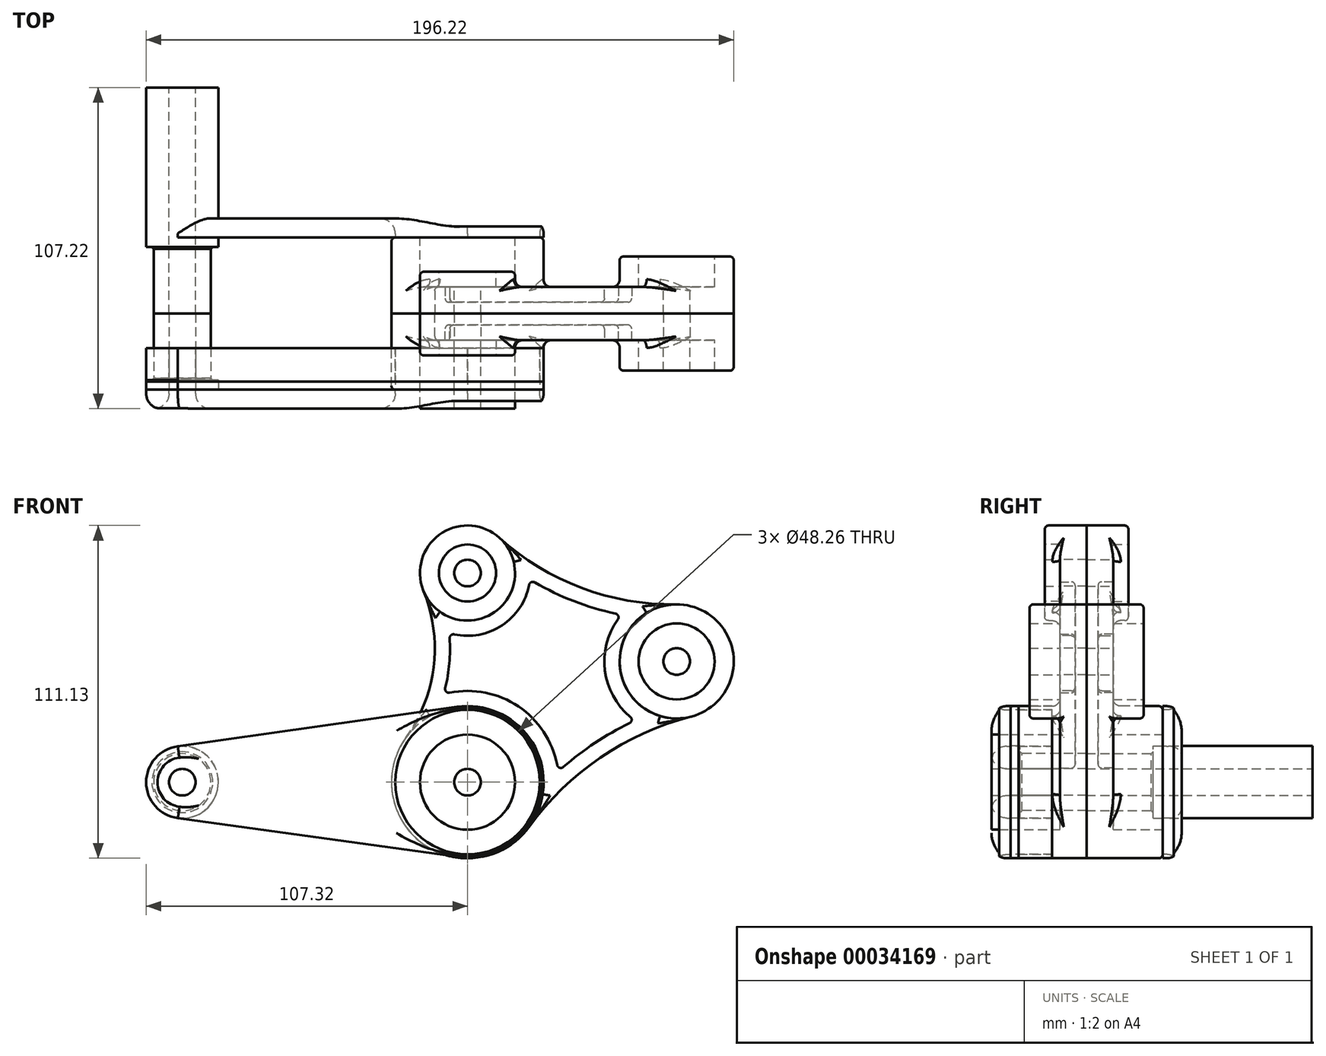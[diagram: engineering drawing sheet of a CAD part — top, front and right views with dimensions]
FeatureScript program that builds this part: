
annotation { "Feature Type Name" : "Feature", "Feature Type Description" : "" }
export const myFeature = defineFeature(function(context is Context, id is Id, definition is map)
    precondition{}
    {
        {
            var Q0;
            Q0=qCreatedBy(makeId("Front.planeOp"),FACE);
            var sketch = newSketch(context, id + "F0", { "sketchPlane" : qUnion([Q0])});
            skCircle(sketch, "E0", {"center": v(0, 0) * mm, "radius": 25.4 * mm});
            skCircle(sketch, "E1", {"center": v(0, 69.85) * mm, "radius": 15.88 * mm});
            skCircle(sketch, "E2", {"center": v(69.85, 40.33) * mm, "radius": 19.05 * mm});
            skLineSegment(sketch, "E3", {"start": v(0, 0) * mm, "end": v(69.85, 40.33) * mm, "construction": true});
            skLineSegment(sketch, "E4", {"start": v(0, 0) * mm, "end": v(74.27, 0) * mm, "construction": true});
            skArc(sketch, "E5", {"start": v(-20.58, 14.89) * mm, "mid": v(-11.3, 38.61) * mm, "end": v(-14.7, 63.85) * mm});
            skArc(sketch, "E6", {"start": v(74.6, 21.88) * mm, "mid": v(44.37, 8.2) * mm, "end": v(20.56, -14.91) * mm});
            skArc(sketch, "E7", {"start": v(10.64, 81.63) * mm, "mid": v(38.02, 64.93) * mm, "end": v(69.6, 59.38) * mm});
            skSolve(sketch);
        }
        {
            var Q0;
            {var subQ0=sQuery(id+"F0.wireOp",EDGE,"E0");var subQ1=sQuery(id+"F0.wireOp",EDGE,"E6");var subQ3=sQuery(id+"F0.wireOp",EDGE,"E5");var subQ4=makeQuery(id+"F0.imprint","INTERSECT",VERTEX,{"derivedFrom":[subQ0,subQ3]});var subQ6=sQuery(id+"F0.wireOp",EDGE,"E1");var subQ9=makeQuery(id+"F0.imprint","INTERSECT",VERTEX,{"derivedFrom":[subQ6,subQ3]});var subQ11=sQuery(id+"F0.wireOp",EDGE,"E2");var subQ13=makeQuery(id+"F0.imprint","INTERSECT",VERTEX,{"derivedFrom":[subQ11,subQ1]});var subQ14=makeQuery(id+"F0.imprint","IMPRINT",EDGE,{"disambiguationData":[TD([[subQ13,1.0]])],"derivedFrom":subQ11});Q0=qUnion([makeQuery(id+"F0.imprint","IMPRINT",FACE,{"disambiguationData":[TD([[makeQuery(id+"F0.imprint","IMPRINT",EDGE,{"disambiguationData":[TD([[subQ4,-1.0]])],"derivedFrom":subQ0}),1.0]])]}),makeQuery(id+"F0.imprint","IMPRINT",FACE,{"disambiguationData":[TD([[makeQuery(id+"F0.imprint","IMPRINT",EDGE,{"disambiguationData":[TD([[subQ9,1.0]])],"derivedFrom":subQ6}),1.0]])]}),makeQuery(id+"F0.imprint","IMPRINT",FACE,{"disambiguationData":[TD([[subQ14,1.0]])]}),makeQuery(id+"F0.imprint","IMPRINT",FACE,{"disambiguationData":[TD([[makeQuery(id+"F0.imprint","IMPRINT",EDGE,{"derivedFrom":subQ3}),-1.0]])]})]);}
            extrude(context, id + "F1", {"entities" : qUnion([Q0]), "depth" : 8.9 * mm});
        }
        {
            var Q0;
            {var subQ0=sQuery(id+"F0.wireOp",EDGE,"E1");var subQ2=makeQuery(id+"F0.imprint","INTERSECT",VERTEX,{"derivedFrom":[subQ0,sQuery(id+"F0.wireOp",EDGE,"E5")]});Q0=makeQuery(id+"F0.imprint","IMPRINT",FACE,{"disambiguationData":[TD([[makeQuery(id+"F0.imprint","IMPRINT",EDGE,{"disambiguationData":[TD([[subQ2,1.0]])],"derivedFrom":subQ0}),1.0]])]});}
            extrude(context, id + "F2", {"entities" : qUnion([Q0]), "operationType" : NewBodyOperationType.ADD, "depth" : 13.97 * mm});
        }
        {
            var Q0;
            {var subQ0=sQuery(id+"F0.wireOp",EDGE,"E2");var subQ2=makeQuery(id+"F0.imprint","INTERSECT",VERTEX,{"derivedFrom":[subQ0,sQuery(id+"F0.wireOp",EDGE,"E6")]});Q0=makeQuery(id+"F0.imprint","IMPRINT",FACE,{"disambiguationData":[TD([[makeQuery(id+"F0.imprint","IMPRINT",EDGE,{"disambiguationData":[TD([[subQ2,1.0]])],"derivedFrom":subQ0}),1.0]])]});}
            extrude(context, id + "F3", {"entities" : qUnion([Q0]), "operationType" : NewBodyOperationType.ADD, "depth" : 19.05 * mm});
        }
        {
            var Q0;
            {var subQ0=sQuery(id+"F0.wireOp",EDGE,"E0");var subQ2=makeQuery(id+"F0.imprint","INTERSECT",VERTEX,{"derivedFrom":[subQ0,sQuery(id+"F0.wireOp",EDGE,"E5")]});Q0=makeQuery(id+"F0.imprint","IMPRINT",FACE,{"disambiguationData":[TD([[makeQuery(id+"F0.imprint","IMPRINT",EDGE,{"disambiguationData":[TD([[subQ2,-1.0]])],"derivedFrom":subQ0}),1.0]])]});}
            extrude(context, id + "F4", {"entities" : qUnion([Q0]), "operationType" : NewBodyOperationType.ADD, "depth" : 25.4 * mm});
        }
        {
            var Q0;
            Q0=makeQuery(id+"F1.opExtrude","CAP_FACE",FACE,{"disambiguationData":[OSD([sQuery(id+"F0.wireOp",EDGE,"E0"),sQuery(id+"F0.wireOp",EDGE,"E1"),sQuery(id+"F0.wireOp",EDGE,"E2"),sQuery(id+"F0.wireOp",EDGE,"E5"),sQuery(id+"F0.wireOp",EDGE,"E6"),sQuery(id+"F0.wireOp",EDGE,"E7")])],"isStart":false});
            var sketch = newSketch(context, id + "F5", { "sketchPlane" : qUnion([Q0])});
            skCircle(sketch, "E8.0", {"center": v(0, 69.85) * mm, "radius": 20.96 * mm});
            skCircle(sketch, "E9.0", {"center": v(69.85, 40.33) * mm, "radius": 24.13 * mm});
            skCircle(sketch, "E10.0", {"center": v(0, 0) * mm, "radius": 30.48 * mm});
            skArc(sketch, "E11.0", {"start": v(-16.46, 11.91) * mm, "mid": v(-6.25, 38) * mm, "end": v(-10, 65.77) * mm});
            skArc(sketch, "E12.0", {"start": v(7.23, 77.86) * mm, "mid": v(36.23, 60.18) * mm, "end": v(69.67, 54.3) * mm});
            skArc(sketch, "E13.0", {"start": v(73.34, 26.8) * mm, "mid": v(41.51, 12.4) * mm, "end": v(16.45, -11.93) * mm});
            skSolve(sketch);
        }
        {
            var Q0;
            {var subQ5=sQuery(id+"F5.wireOp",EDGE,"E12.0");var subQ7=sQuery(id+"F5.wireOp",EDGE,"E8.0");var subQ8=makeQuery(id+"F5.imprint","INTERSECT",VERTEX,{"derivedFrom":[subQ7,subQ5]});Q0=makeQuery(id+"F5.imprint","IMPRINT",FACE,{"disambiguationData":[TD([[makeQuery(id+"F5.imprint","IMPRINT",EDGE,{"disambiguationData":[TD([[subQ8,1.0]])],"derivedFrom":subQ7}),-1.0]])]});}
            extrude(context, id + "F6", {"entities" : qUnion([Q0]), "operationType" : NewBodyOperationType.REMOVE, "oppositeDirection" : true, "depth" : 5.08 * mm});
        }
        {
            var Q0;
            Q0=makeQuery(id+"F4.opExtrude","CAP_FACE",FACE,{"disambiguationData":[OSD([sQuery(id+"F0.wireOp",EDGE,"E0")])],"isStart":false});
            var sketch = newSketch(context, id + "F7", { "sketchPlane" : qUnion([Q0])});
            skCircle(sketch, "E14", {"center": v(0, 0) * mm, "radius": 15.88 * mm});
            skCircle(sketch, "E15.0", {"center": v(0, 69.85) * mm, "radius": 15.88 * mm, "construction": true});
            skCircle(sketch, "E15.1", {"center": v(69.85, 40.33) * mm, "radius": 19.05 * mm, "construction": true});
            skCircle(sketch, "E16", {"center": v(0, 69.85) * mm, "radius": 9.53 * mm});
            skCircle(sketch, "E17", {"center": v(69.85, 40.33) * mm, "radius": 12.7 * mm});
            skSolve(sketch);
        }
        {
            var Q0;
            Q0=makeQuery(id+"F7.imprint","IMPRINT",FACE,{"disambiguationData":[TD([[makeQuery(id+"F7.imprint","IMPRINT",EDGE,{"derivedFrom":sQuery(id+"F7.wireOp",EDGE,"E14")}),1.0]])]});
            var Q1;
            Q1=makeQuery(id+"F7.imprint","IMPRINT",FACE,{"disambiguationData":[TD([[makeQuery(id+"F7.imprint","IMPRINT",EDGE,{"derivedFrom":sQuery(id+"F7.wireOp",EDGE,"E16")}),1.0]])]});
            var Q2;
            Q2=makeQuery(id+"F7.imprint","IMPRINT",FACE,{"disambiguationData":[TD([[makeQuery(id+"F7.imprint","IMPRINT",EDGE,{"derivedFrom":sQuery(id+"F7.wireOp",EDGE,"E17")}),1.0]])]});
            var Q3;
            Q3=makeQuery(id+"F1.opExtrude","CAP_FACE",FACE,{"disambiguationData":[OSD([sQuery(id+"F0.wireOp",EDGE,"E0"),sQuery(id+"F0.wireOp",EDGE,"E1"),sQuery(id+"F0.wireOp",EDGE,"E2"),sQuery(id+"F0.wireOp",EDGE,"E5"),sQuery(id+"F0.wireOp",EDGE,"E6"),sQuery(id+"F0.wireOp",EDGE,"E7")])],"isStart":false});
            extrude(context, id + "F8", {"entities" : qUnion([Q0, Q1, Q2]), "operationType" : NewBodyOperationType.REMOVE, "endBound" : BoundingType.UP_TO_SURFACE, "oppositeDirection" : true, "endBoundEntityFace" : qUnion([Q3]), "depth" : 25.4 * mm});
        }
        {
            var Q0;
            Q0=makeQuery(id+"F8.boolean.opBoolean","COPY",FACE,{"derivedFrom":makeQuery(id+"F8.opExtrude","CAP_FACE",FACE,{"disambiguationData":[OSD([sQuery(id+"F7.wireOp",EDGE,"E17")])],"isStart":false})});
            var sketch = newSketch(context, id + "F9", { "sketchPlane" : qUnion([Q0])});
            skCircle(sketch, "E18.0", {"center": v(0, 69.85) * mm, "radius": 9.53 * mm});
            skCircle(sketch, "E18.1", {"center": v(0, 0) * mm, "radius": 15.88 * mm});
            skCircle(sketch, "E18.2", {"center": v(69.85, 40.33) * mm, "radius": 12.7 * mm});
            skCircle(sketch, "E19", {"center": v(0, 0) * mm, "radius": 4.45 * mm});
            skCircle(sketch, "E20", {"center": v(0, 69.85) * mm, "radius": 4.45 * mm});
            skCircle(sketch, "E21", {"center": v(69.85, 40.33) * mm, "radius": 4.45 * mm});
            skSolve(sketch);
        }
        {
            var Q0;
            Q0=makeQuery(id+"F9.imprint","IMPRINT",FACE,{"disambiguationData":[TD([[makeQuery(id+"F9.imprint","IMPRINT",EDGE,{"derivedFrom":sQuery(id+"F9.wireOp",EDGE,"E20")}),1.0]])]});
            var Q1;
            Q1=makeQuery(id+"F9.imprint","IMPRINT",FACE,{"disambiguationData":[TD([[makeQuery(id+"F9.imprint","IMPRINT",EDGE,{"derivedFrom":sQuery(id+"F9.wireOp",EDGE,"E21")}),1.0]])]});
            var Q2;
            Q2=makeQuery(id+"F9.imprint","IMPRINT",FACE,{"disambiguationData":[TD([[makeQuery(id+"F9.imprint","IMPRINT",EDGE,{"derivedFrom":sQuery(id+"F9.wireOp",EDGE,"E19")}),1.0]])]});
            extrude(context, id + "F10", {"entities" : qUnion([Q0, Q1, Q2]), "operationType" : NewBodyOperationType.REMOVE, "endBound" : BoundingType.THROUGH_ALL, "oppositeDirection" : true, "depth" : 25.4 * mm});
        }
        {
            var Q0;
            Q0=makeQuery(id+"F6.boolean.opBoolean","COPY",FACE,{"derivedFrom":makeQuery(id+"F6.opExtrude","CAP_FACE",FACE,{"disambiguationData":[OSD([sQuery(id+"F5.wireOp",EDGE,"E8.0"),sQuery(id+"F5.wireOp",EDGE,"E9.0"),sQuery(id+"F5.wireOp",EDGE,"E10.0"),sQuery(id+"F5.wireOp",EDGE,"E11.0"),sQuery(id+"F5.wireOp",EDGE,"E12.0"),sQuery(id+"F5.wireOp",EDGE,"E13.0")])],"isStart":false})});
            var Q1;
            Q1=makeQuery(id+"F6.boolean.opBoolean","COPY",EDGE,{"derivedFrom":makeQuery(id+"F6.opExtrude","SWEPT_EDGE",EDGE,{"disambiguationData":[OSD([sQuery(id+"F5.wireOp",EDGE,"E8.0"),sQuery(id+"F5.wireOp",EDGE,"E11.0")])]})});
            var Q2;
            Q2=makeQuery(id+"F6.boolean.opBoolean","COPY",EDGE,{"derivedFrom":makeQuery(id+"F6.opExtrude","SWEPT_EDGE",EDGE,{"disambiguationData":[OSD([sQuery(id+"F5.wireOp",EDGE,"E8.0"),sQuery(id+"F5.wireOp",EDGE,"E12.0")])]})});
            var Q3;
            Q3=makeQuery(id+"F6.boolean.opBoolean","COPY",EDGE,{"derivedFrom":makeQuery(id+"F6.opExtrude","SWEPT_EDGE",EDGE,{"disambiguationData":[OSD([sQuery(id+"F5.wireOp",EDGE,"E9.0"),sQuery(id+"F5.wireOp",EDGE,"E12.0")])]})});
            var Q4;
            Q4=makeQuery(id+"F6.boolean.opBoolean","COPY",EDGE,{"derivedFrom":makeQuery(id+"F6.opExtrude","SWEPT_EDGE",EDGE,{"disambiguationData":[OSD([sQuery(id+"F5.wireOp",EDGE,"E9.0"),sQuery(id+"F5.wireOp",EDGE,"E13.0")])]})});
            var Q5;
            Q5=makeQuery(id+"F6.boolean.opBoolean","COPY",EDGE,{"derivedFrom":makeQuery(id+"F6.opExtrude","SWEPT_EDGE",EDGE,{"disambiguationData":[OSD([sQuery(id+"F5.wireOp",EDGE,"E10.0"),sQuery(id+"F5.wireOp",EDGE,"E13.0")])]})});
            var Q6;
            Q6=makeQuery(id+"F6.boolean.opBoolean","COPY",EDGE,{"derivedFrom":makeQuery(id+"F6.opExtrude","SWEPT_EDGE",EDGE,{"disambiguationData":[OSD([sQuery(id+"F5.wireOp",EDGE,"E10.0"),sQuery(id+"F5.wireOp",EDGE,"E11.0")])]})});
            var Q7;
            Q7=makeQuery(id+"F6.boolean.opBoolean","COPY",EDGE,{"derivedFrom":makeQuery(id+"F6.opExtrude","CAP_EDGE",EDGE,{"disambiguationData":[OSD([sQuery(id+"F5.wireOp",EDGE,"E10.0")])],"isStart":true})});
            var Q8;
            Q8=makeQuery(id+"F1.opExtrude","CAP_EDGE",EDGE,{"disambiguationData":[OSD([sQuery(id+"F0.wireOp",EDGE,"E7")])],"isStart":false});
            var Q9;
            Q9=makeQuery(id+"F1.opExtrude","CAP_EDGE",EDGE,{"disambiguationData":[OSD([sQuery(id+"F0.wireOp",EDGE,"E6")])],"isStart":false});
            var Q10;
            Q10=makeQuery(id+"F1.opExtrude","CAP_EDGE",EDGE,{"disambiguationData":[OSD([sQuery(id+"F0.wireOp",EDGE,"E5")])],"isStart":false});
            var Q11;
            Q11=makeQuery(id+"F4.opExtrude","CAP_EDGE",EDGE,{"disambiguationData":[OSD([sQuery(id+"F0.wireOp",EDGE,"E0")])],"isStart":false});
            var Q12;
            Q12=makeQuery(id+"F3.opExtrude","CAP_EDGE",EDGE,{"disambiguationData":[OSD([sQuery(id+"F0.wireOp",EDGE,"E2")])],"isStart":false});
            var Q13;
            Q13=makeQuery(id+"F2.opExtrude","CAP_EDGE",EDGE,{"disambiguationData":[OSD([sQuery(id+"F0.wireOp",EDGE,"E1")])],"isStart":false});
            fillet(context, id + "F11", {"entities" : qUnion([Q0, Q1, Q2, Q3, Q4, Q5, Q6, Q7, Q8, Q9, Q10, Q11, Q12, Q13]), "radius" : 1.27 * mm, "tangentPropagation" : true, "allowEdgeOverflow" : false});
        }
        {
            var Q0;
            {var subQ0=sQuery(id+"F0.wireOp",EDGE,"E2");Q0=makeQuery(id+"F3.boolean.opBoolean","INTERSECT",EDGE,{"derivedFrom":[makeQuery(id+"F1.opExtrude","CAP_FACE",FACE,{"disambiguationData":[OSD([sQuery(id+"F0.wireOp",EDGE,"E0"),sQuery(id+"F0.wireOp",EDGE,"E1"),subQ0,sQuery(id+"F0.wireOp",EDGE,"E5"),sQuery(id+"F0.wireOp",EDGE,"E6"),sQuery(id+"F0.wireOp",EDGE,"E7")])],"isStart":false}),makeQuery(id+"F3.opExtrude","SWEPT_FACE",FACE,{"disambiguationData":[OSD([subQ0])]})]});}
            var Q1;
            {var subQ0=sQuery(id+"F0.wireOp",EDGE,"E0");Q1=makeQuery(id+"F4.boolean.opBoolean","INTERSECT",EDGE,{"derivedFrom":[makeQuery(id+"F1.opExtrude","CAP_FACE",FACE,{"disambiguationData":[OSD([subQ0,sQuery(id+"F0.wireOp",EDGE,"E1"),sQuery(id+"F0.wireOp",EDGE,"E2"),sQuery(id+"F0.wireOp",EDGE,"E5"),sQuery(id+"F0.wireOp",EDGE,"E6"),sQuery(id+"F0.wireOp",EDGE,"E7")])],"isStart":false}),makeQuery(id+"F4.opExtrude","SWEPT_FACE",FACE,{"disambiguationData":[OSD([subQ0])]})]});}
            var Q2;
            {var subQ0=sQuery(id+"F0.wireOp",EDGE,"E1");Q2=makeQuery(id+"F2.boolean.opBoolean","INTERSECT",EDGE,{"derivedFrom":[makeQuery(id+"F1.opExtrude","CAP_FACE",FACE,{"disambiguationData":[OSD([sQuery(id+"F0.wireOp",EDGE,"E0"),subQ0,sQuery(id+"F0.wireOp",EDGE,"E2"),sQuery(id+"F0.wireOp",EDGE,"E5"),sQuery(id+"F0.wireOp",EDGE,"E6"),sQuery(id+"F0.wireOp",EDGE,"E7")])],"isStart":false}),makeQuery(id+"F2.opExtrude","SWEPT_FACE",FACE,{"disambiguationData":[OSD([subQ0])]})]});}
            fillet(context, id + "F12", {"entities" : qUnion([Q0, Q1, Q2]), "radius" : 2.54 * mm, "tangentPropagation" : true, "allowEdgeOverflow" : false});
        }
        {
            var Q0;
            Q0=makeQuery(id+"F1.opExtrude","SWEPT_BODY",BODY,{"disambiguationData":[OSD([sQuery(id+"F0.wireOp",EDGE,"E0"),sQuery(id+"F0.wireOp",EDGE,"E1"),sQuery(id+"F0.wireOp",EDGE,"E2"),sQuery(id+"F0.wireOp",EDGE,"E5"),sQuery(id+"F0.wireOp",EDGE,"E6"),sQuery(id+"F0.wireOp",EDGE,"E7")])]});
            var Q1;
            Q1=qCreatedBy(makeId("Front.planeOp"),FACE);
            mirror(context, id + "F13", {"entities" : qUnion([Q0]), "mirrorPlane" : qUnion([Q1])});
        }
        {
            var Q0;
            Q0=makeQuery(id+"F8.boolean.opBoolean","COPY",FACE,{"derivedFrom":makeQuery(id+"F8.opExtrude","CAP_FACE",FACE,{"disambiguationData":[OSD([sQuery(id+"F7.wireOp",EDGE,"E16")])],"isStart":false})});
            var sketch = newSketch(context, id + "F14", { "sketchPlane" : qUnion([Q0])});
            skCircle(sketch, "E22.0.0", {"center": v(0, 69.85) * mm, "radius": 9.53 * mm});
            skSolve(sketch);
        }
        {
            var Q0;
            Q0=makeQuery(id+"F14.imprint","IMPRINT",FACE,{"disambiguationData":[TD([[makeQuery(id+"F14.imprint","IMPRINT",EDGE,{"derivedFrom":sQuery(id+"F14.wireOp",EDGE,"E22.0.0")}),-1.0]])]});
            var Q1;
            Q1=makeQuery(id+"F2.opExtrude","CAP_FACE",FACE,{"disambiguationData":[OSD([sQuery(id+"F0.wireOp",EDGE,"E1")])],"isStart":false});
            extrude(context, id + "F15", {"entities" : qUnion([Q0]), "endBound" : BoundingType.UP_TO_SURFACE, "endBoundEntityFace" : qUnion([Q1]), "depth" : 25.4 * mm});
        }
        {
            var Q0;
            Q0=makeQuery(id+"F8.boolean.opBoolean","COPY",FACE,{"derivedFrom":makeQuery(id+"F8.opExtrude","CAP_FACE",FACE,{"disambiguationData":[OSD([sQuery(id+"F7.wireOp",EDGE,"E17")])],"isStart":false})});
            var Q1;
            Q1=makeQuery(id+"F3.opExtrude","CAP_FACE",FACE,{"disambiguationData":[OSD([sQuery(id+"F0.wireOp",EDGE,"E2")])],"isStart":false});
            extrude(context, id + "F16", {"entities" : qUnion([Q0]), "endBound" : BoundingType.UP_TO_SURFACE, "endBoundEntityFace" : qUnion([Q1]), "depth" : 25.4 * mm});
        }
        {
            var Q0;
            Q0=makeQuery(id+"F8.boolean.opBoolean","COPY",FACE,{"derivedFrom":makeQuery(id+"F8.opExtrude","CAP_FACE",FACE,{"disambiguationData":[OSD([sQuery(id+"F7.wireOp",EDGE,"E14")])],"isStart":false})});
            var sketch = newSketch(context, id + "F17", { "sketchPlane" : qUnion([Q0])});
            skCircle(sketch, "E23.0", {"center": v(0, 0) * mm, "radius": 4.45 * mm});
            skCircle(sketch, "E23.1", {"center": v(0, 0) * mm, "radius": 15.88 * mm});
            skSolve(sketch);
        }
        {
            var Q0;
            Q0=makeQuery(id+"F17.imprint","IMPRINT",FACE,{"disambiguationData":[TD([[makeQuery(id+"F17.imprint","IMPRINT",EDGE,{"derivedFrom":sQuery(id+"F17.wireOp",EDGE,"E23.0")}),-1.0]])]});
            var Q1;
            Q1=makeQuery(id+"F4.opExtrude","CAP_FACE",FACE,{"disambiguationData":[OSD([sQuery(id+"F0.wireOp",EDGE,"E0")])],"isStart":false});
            extrude(context, id + "F18", {"entities" : qUnion([Q0]), "endBound" : BoundingType.UP_TO_SURFACE, "endBoundEntityFace" : qUnion([Q1]), "depth" : 25.4 * mm});
        }
        {
            var Q0;
            Q0=qCreatedBy(makeId("Top.planeOp"),FACE);
            var sketch = newSketch(context, id + "F19", { "sketchPlane" : qUnion([Q0])});
            skLineSegment(sketch, "E24", {"start": v(-90.8, 0) * mm, "end": v(-90.8, -25.4) * mm});
            skLineSegment(sketch, "E25", {"start": v(-90.8, -25.4) * mm, "end": v(-83.19, -25.4) * mm});
            skLineSegment(sketch, "E26", {"start": v(-83.19, -25.4) * mm, "end": v(-83.19, -22.23) * mm});
            skLineSegment(sketch, "E27", {"start": v(-83.19, -22.23) * mm, "end": v(-85.1, -22.23) * mm});
            skLineSegment(sketch, "E28", {"start": v(-85.1, -22.23) * mm, "end": v(-85.73, -21.6) * mm});
            skLineSegment(sketch, "E29", {"start": v(-85.73, -21.6) * mm, "end": v(-85.73, 0) * mm});
            skLineSegment(sketch, "E30", {"start": v(-85.73, 0) * mm, "end": v(-90.8, 0) * mm});
            skLineSegment(sketch, "E31.0", {"start": v(24.13, -25.4) * mm, "end": v(-24.13, -25.4) * mm});
            skLineSegment(sketch, "E32", {"start": v(-95.25, -25.4) * mm, "end": v(-95.25, 0) * mm, "construction": true});
            skSolve(sketch);
        }
        {
            var Q0;
            Q0=makeQuery(id+"F19.imprint","IMPRINT",FACE,{"disambiguationData":[TD([[makeQuery(id+"F19.imprint","IMPRINT",EDGE,{"derivedFrom":sQuery(id+"F19.wireOp",EDGE,"E24")}),1.0]])]});
            var Q1;
            Q1=sQuery(id+"F19.wireOp",EDGE,"E32");
            revolve(context, id + "F20", {"entities" : qUnion([Q0]), "axis" : qUnion([Q1]), "revolveType" : RevolveType.FULL});
        }
        {
            var Q0;
            Q0=makeQuery(id+"F20.opRevolve","SWEPT_BODY",BODY,{"disambiguationData":[OSD([sQuery(id+"F19.wireOp",EDGE,"E24"),sQuery(id+"F19.wireOp",EDGE,"E25"),sQuery(id+"F19.wireOp",EDGE,"E26"),sQuery(id+"F19.wireOp",EDGE,"E27"),sQuery(id+"F19.wireOp",EDGE,"E28"),sQuery(id+"F19.wireOp",EDGE,"E29"),sQuery(id+"F19.wireOp",EDGE,"E30")])]});
            var Q1;
            Q1=makeQuery(id+"F20.opRevolve","SWEPT_FACE",FACE,{"disambiguationData":[OSD([sQuery(id+"F19.wireOp",EDGE,"E30")])]});
            mirror(context, id + "F21", {"entities" : qUnion([Q0]), "mirrorPlane" : qUnion([Q1])});
        }
        {
            var Q0;
            Q0=makeQuery(id+"F4.opExtrude","CAP_FACE",FACE,{"disambiguationData":[OSD([sQuery(id+"F0.wireOp",EDGE,"E0")])],"isStart":false});
            var sketch = newSketch(context, id + "F22", { "sketchPlane" : qUnion([Q0])});
            skCircle(sketch, "E33.0", {"center": v(-95.25, 0) * mm, "radius": 12.07 * mm});
            skArc(sketch, "E34.0", {"start": v(-96.74, 11.97) * mm, "mid": v(-107.31, -0.03) * mm, "end": v(-96.7, -11.98) * mm});
            skCircle(sketch, "E34.1", {"center": v(-95.25, 0) * mm, "radius": 4.45 * mm});
            skCircle(sketch, "E35.2", {"center": v(0, 0) * mm, "radius": 25.4 * mm});
            skArc(sketch, "E36.2", {"start": v(-6.92, -24.44) * mm, "mid": v(25.34, -1.72) * mm, "end": v(-3.56, 25.15) * mm});
            skCircle(sketch, "E36.3", {"center": v(0, 0) * mm, "radius": 4.45 * mm});
            skLineSegment(sketch, "E37", {"start": v(-96.74, 11.97) * mm, "end": v(-3.56, 25.15) * mm});
            skLineSegment(sketch, "E38", {"start": v(-96.7, -11.98) * mm, "end": v(0, -25.4) * mm});
            skSolve(sketch);
        }
        {
            var Q0;
            {var subQ0=sQuery(id+"F0.wireOp",EDGE,"E0");Q0=makeQuery(id+"F22.imprint","IMPRINT",FACE,{"disambiguationData":[TD([[makeQuery(id+"F22.imprint","IMPRINT",EDGE,{"derivedFrom":makeQuery(id+"F11.opFillet","BLEND_EDGE",EDGE,{"blendedFrom":[makeQuery(id+"F4.opExtrude","CAP_EDGE",EDGE,{"disambiguationData":[OSD([subQ0])],"isStart":false}),makeQuery(id+"F4.opExtrude","CAP_FACE",FACE,{"disambiguationData":[OSD([subQ0])],"isStart":false})],"blendedInto":[makeQuery(id+"F4.opExtrude","CAP_FACE",FACE,{"disambiguationData":[OSD([subQ0])],"isStart":false})]})}),-1.0]])]});}
            var Q1;
            {var subQ0=sQuery(id+"F22.wireOp",EDGE,"E38");var subQ1=sQuery(id+"F22.wireOp",EDGE,"E35.2");var subQ3=makeQuery(id+"F22.imprint","INTERSECT",VERTEX,{"disambiguationData":[OD(0.0)],"derivedFrom":[subQ1,subQ0]});Q1=makeQuery(id+"F22.imprint","IMPRINT",FACE,{"disambiguationData":[TD([[makeQuery(id+"F22.imprint","IMPRINT",EDGE,{"disambiguationData":[TD([[subQ3,1.0]])],"derivedFrom":subQ1}),1.0]])]});}
            var Q2;
            Q2=makeQuery(id+"F22.imprint","IMPRINT",FACE,{"disambiguationData":[TD([[makeQuery(id+"F22.imprint","IMPRINT",EDGE,{"derivedFrom":sQuery(id+"F22.wireOp",EDGE,"E34.1")}),-1.0]])]});
            var Q3;
            {var subQ5=sQuery(id+"F22.wireOp",EDGE,"E37");Q3=makeQuery(id+"F22.imprint","IMPRINT",FACE,{"disambiguationData":[TD([[makeQuery(id+"F22.imprint","IMPRINT",EDGE,{"derivedFrom":subQ5}),-1.0]])]});}
            var Q4;
            Q4=makeQuery(id+"F22.imprint","IMPRINT",FACE,{"disambiguationData":[TD([[makeQuery(id+"F22.imprint","IMPRINT",EDGE,{"derivedFrom":makeQuery(id+"F8.boolean.opBoolean","COPY",EDGE,{"derivedFrom":makeQuery(id+"F8.opExtrude","CAP_EDGE",EDGE,{"disambiguationData":[OSD([sQuery(id+"F7.wireOp",EDGE,"E14")])],"isStart":true})})}),-1.0]])]});
            var Q5;
            Q5=makeQuery(id+"F22.imprint","IMPRINT",FACE,{"disambiguationData":[TD([[makeQuery(id+"F22.imprint","IMPRINT",EDGE,{"derivedFrom":sQuery(id+"F22.wireOp",EDGE,"E36.3")}),-1.0]])]});
            extrude(context, id + "F23", {"entities" : qUnion([Q0, Q1, Q2, Q3, Q4, Q5]), "depth" : 6.35 * mm});
        }
        {
            var Q0;
            Q0=makeQuery(id+"F23.opExtrude","CAP_FACE",FACE,{"disambiguationData":[OSD([sQuery(id+"F22.wireOp",EDGE,"E35.2"),sQuery(id+"F22.wireOp",EDGE,"E33.0"),sQuery(id+"F22.wireOp",EDGE,"E34.1"),sQuery(id+"F22.wireOp",EDGE,"E36.3"),sQuery(id+"F22.wireOp",EDGE,"E37"),sQuery(id+"F22.wireOp",EDGE,"E38")])],"isStart":false});
            fillet(context, id + "F24", {"entities" : qUnion([Q0]), "radius" : 5.08 * mm, "tangentPropagation" : true, "allowEdgeOverflow" : false});
        }
        {
            var Q0;
            Q0=makeQuery(id+"F23.opExtrude","SWEPT_BODY",BODY,{"disambiguationData":[OSD([sQuery(id+"F22.wireOp",EDGE,"E35.2"),sQuery(id+"F22.wireOp",EDGE,"E33.0"),sQuery(id+"F22.wireOp",EDGE,"E34.1"),sQuery(id+"F22.wireOp",EDGE,"E36.3"),sQuery(id+"F22.wireOp",EDGE,"E37"),sQuery(id+"F22.wireOp",EDGE,"E38")])]});
            var Q1;
            Q1=qCreatedBy(makeId("Front.planeOp"),FACE);
            mirror(context, id + "F25", {"entities" : qUnion([Q0]), "mirrorPlane" : qUnion([Q1])});
        }
        {
            var Q0;
            Q0=makeQuery(id+"F23.opExtrude","CAP_FACE",FACE,{"disambiguationData":[OSD([sQuery(id+"F22.wireOp",EDGE,"E35.2"),sQuery(id+"F22.wireOp",EDGE,"E33.0"),sQuery(id+"F22.wireOp",EDGE,"E34.1"),sQuery(id+"F22.wireOp",EDGE,"E36.3"),sQuery(id+"F22.wireOp",EDGE,"E37"),sQuery(id+"F22.wireOp",EDGE,"E38")])],"isStart":true});
            extrude(context, id + "F26", {"entities" : qUnion([Q0]), "depth" : 13.9 * mm});
        }
        {
            var Q0;
            Q0=makeQuery(id+"F26.opExtrude","CAP_FACE",FACE,{"disambiguationData":[OSD([sQuery(id+"F22.wireOp",EDGE,"E35.2"),sQuery(id+"F22.wireOp",EDGE,"E33.0"),sQuery(id+"F22.wireOp",EDGE,"E34.1"),sQuery(id+"F22.wireOp",EDGE,"E36.3"),sQuery(id+"F22.wireOp",EDGE,"E37"),sQuery(id+"F22.wireOp",EDGE,"E38")])],"isStart":false});
            extrude(context, id + "F27", {"entities" : qUnion([Q0]), "oppositeDirection" : true, "depth" : 11.26 * mm});
        }
        {
            var Q0;
            Q0=makeQuery(id+"F21.opPattern","COPY",FACE,{"derivedFrom":makeQuery(id+"F20.opRevolve","SWEPT_FACE",FACE,{"disambiguationData":[OSD([sQuery(id+"F19.wireOp",EDGE,"E25")])]}),"instanceName":"1"});
            extrude(context, id + "F28", {"entities" : qUnion([Q0]), "operationType" : NewBodyOperationType.ADD, "depth" : 50.07 * mm});
        }
    });
